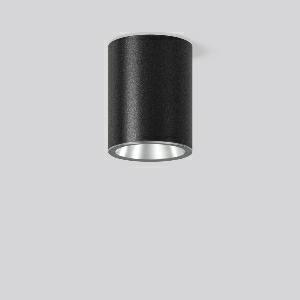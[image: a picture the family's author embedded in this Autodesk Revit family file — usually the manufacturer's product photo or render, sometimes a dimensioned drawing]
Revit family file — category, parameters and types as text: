
# Revit family: andho_mini_931251_0031_f819
name_source: partatom
category: Lighting Fixtures
units: mm (PartAtom-declared; Revit-internal decimal feet)

## family parameters
Cut with Voids When Loaded = No
Host = Face
Light Source = No
Part Type = Normal
Room Calculation Point = No
Round Connector Dimension = Use Diameter
Shared = No

## types (1)
- ANDHO mini (1 x LED Modul 830, 1550 lm, 3000)
    Apparent Load = 13 VA
    CIE Flux Codes = 96 100 100 100 100
    Color Rendering = 80
    Color Temperature = 3000
    Default Elevation = 1800 mm
    Description = Series: ANDHO mini
High-quality surface-mounted downlight for indoor and outdoor use. Housing made of corrosion-resistant die-cast aluminium, seawater resistant powder-coated. With membrane valve as a standard to avoid condensed water. Cover clear single-pane toughened glass. Rotation-symmetric reflector made of reflex-boosted MIRO-SILVER. Easy installation with a separate ceiling frame and plug connection. 5 pole double terminal for through-wiring. 
Colour: anthracite metallic (DB703)
Diameter: 114 mm
Height: 147 mm
Lamp: LED
Socket: without socket
Colour temperature: 3000K
Colour rendering index (CRI): 80
System power: 13 W
Rated luminous flux: 1550 lm
Beam angle Down: 40°
Luminous efficiency: 119 lm/W
Control gear: Regulated power supply
Protection class: I
Type of protection: IP 66
    Height = 147 mm
    Lamp = 1 x LED Modul 830
    Lamp Light Flux = 1550 lm
    Lamp count = 1
    Length = 114 mm
    Lifetime = 50000 h
    Luminous efficacy = 119 lm/W
    Manufacturer = RZB
    ModVariant = No
    Model = 931251.0031
    Mounting Place = Ceiling
    Mounting Type = Surface mounted
    Number of Poles = 1
    OnlyDefault = Yes
    Power Factor = 1
    Product Name = ANDHO mini
    Product group = Surface mounted downlights
    ProductGroupID = 302
    Protection Class = Protection class I
    Protection Degree = Degree of protection
    RLX_Detail_Level = 1
    RLX_Emergency_Light_Flux = 0 lm
    RLX_Emergency_Type = 0
    RLX_Emergency_Type_DB = No
    RlxData = <blob elided: 27013 chars, md5=3233353f>
    Socket = socket
    Standby Power = 0 W
    System Light Flux = 1550 lm
    System Power = 13 W
    Type Comments = ALEA SPOT
    Type Image = 931251.0031.jpg
    URL = http://relux.com
    VarID = ---
    Voltage = 0 V
    Weight = 0.00 kg
    Width = 0 mm  [stored 0 ft]

note: [stored X ft] marks values corroborated as IEEE doubles in the binary element streams (Revit-internal decimal feet)

## geometry (parser evidence)
native form markers: Blend x4, Sweep x12
no freeform markers — native parametric forms only
